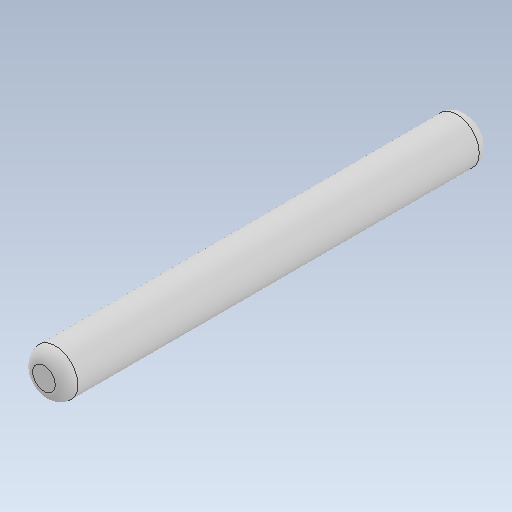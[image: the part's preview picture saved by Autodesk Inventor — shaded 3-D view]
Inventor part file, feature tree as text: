
AUTODESK INVENTOR PART (.ipt)
format: ipt  version: 2020 (Build 240168000, 168)  size: 90,112 bytes
history: native  units: in
note: dims shown in document units (in); Inventor stores cm internally (conversion verified against a paired STEP export)
features: fillet x1
ambient origin geometry x8: Origin, YZ Plane, XZ Plane, XY Plane, X Axis, Y Axis, Z Axis, Center Point
bodies: Solid1 (feature_tree)
feature tree (1):
  fillet  "Fillet1"  [1 undecoded]
note: 1 required parameter value undecoded (feature->parameter linkage not recoverable at this tier; creation-order binding heuristic only, values carry confidence <= 0.55)
